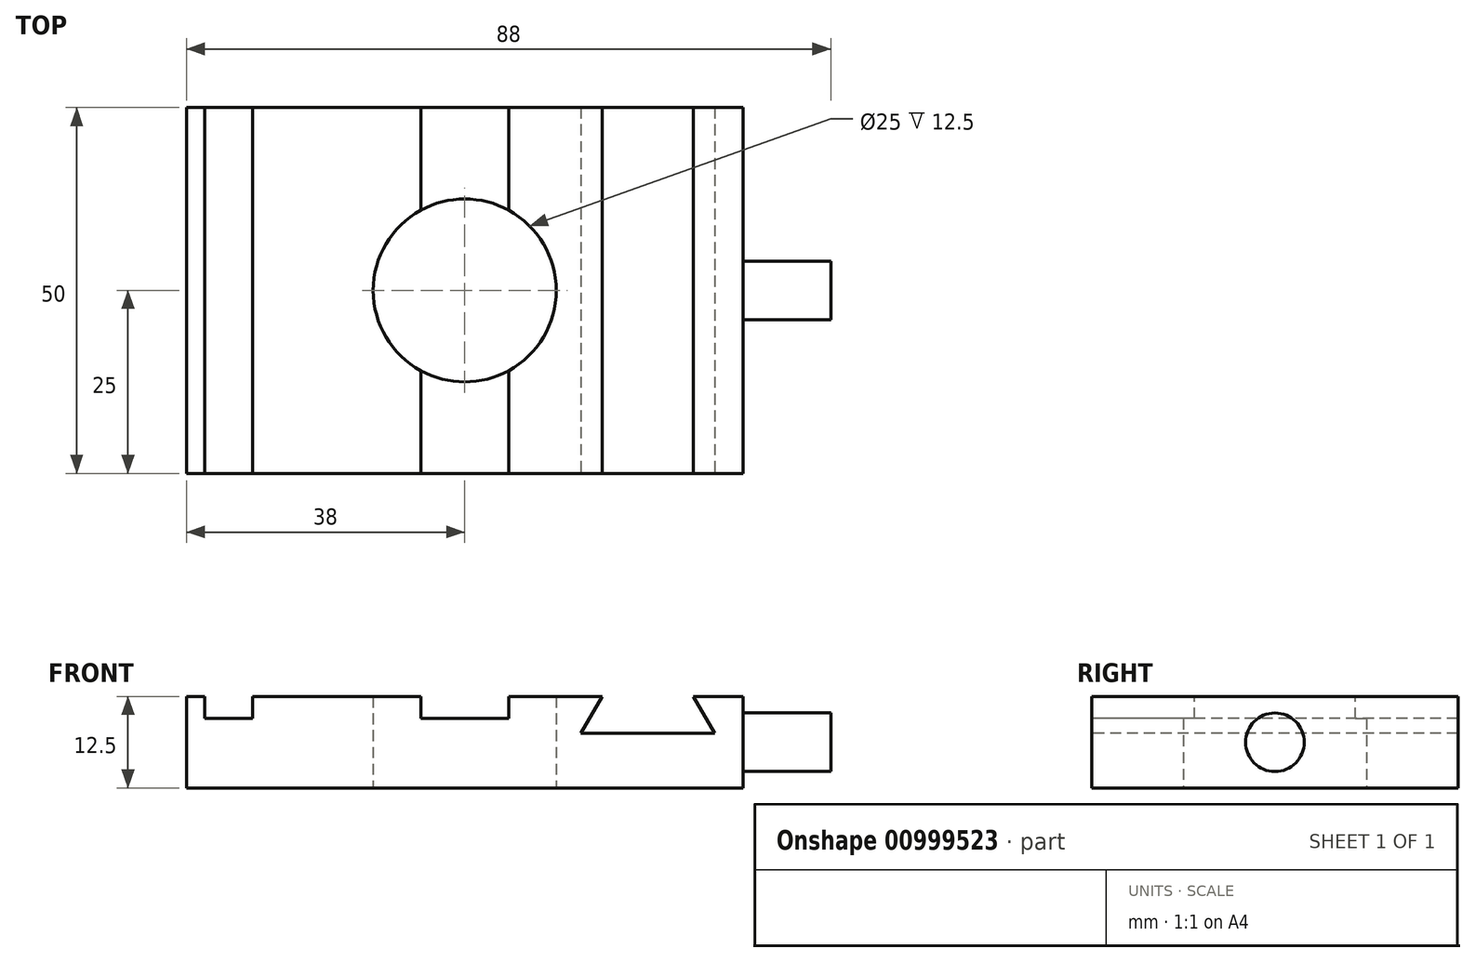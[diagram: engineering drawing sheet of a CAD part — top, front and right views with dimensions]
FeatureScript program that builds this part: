
annotation { "Feature Type Name" : "Feature", "Feature Type Description" : "" }
export const myFeature = defineFeature(function(context is Context, id is Id, definition is map)
    precondition{}
    {
        {
            var Q0;
            Q0=qCreatedBy(makeId("Top.planeOp"),FACE);
            var sketch = newSketch(context, id + "F0", { "sketchPlane" : qUnion([Q0])});
            skLineSegment(sketch, "E0.bottom", {"start": v(38, 25) * mm, "end": v(-38, 25) * mm});
            skLineSegment(sketch, "E0.top", {"start": v(38, -25) * mm, "end": v(-38, -25) * mm});
            skLineSegment(sketch, "E0.left", {"start": v(38, 25) * mm, "end": v(38, -25) * mm});
            skLineSegment(sketch, "E0.right", {"start": v(-38, 25) * mm, "end": v(-38, -25) * mm});
            skPoint(sketch, "E0.middle", {"position": v(0, 0) * mm});
            skCircle(sketch, "E1", {"center": v(0, 0) * mm, "radius": 12.5 * mm});
            skSolve(sketch);
        }
        {
            var Q0;
            Q0=makeQuery(id+"F0.imprint","IMPRINT",FACE,{"disambiguationData":[TD([[makeQuery(id+"F0.imprint","IMPRINT",EDGE,{"derivedFrom":sQuery(id+"F0.wireOp",EDGE,"E0.bottom")}),1.0]])]});
            extrude(context, id + "F1", {"entities" : qUnion([Q0]), "depth" : 12.5 * mm, "offsetDistance" : 25 * mm});
        }
        {
            var Q0;
            Q0=makeQuery(id+"F1.opExtrude","CAP_FACE",FACE,{"disambiguationData":[OSD([sQuery(id+"F0.wireOp",EDGE,"E0.bottom"),sQuery(id+"F0.wireOp",EDGE,"E0.top"),sQuery(id+"F0.wireOp",EDGE,"E0.left"),sQuery(id+"F0.wireOp",EDGE,"E0.right"),sQuery(id+"F0.wireOp",EDGE,"E1")])],"isStart":false});
            var sketch = newSketch(context, id + "F2", { "sketchPlane" : qUnion([Q0])});
            skLineSegment(sketch, "E2.bottom", {"start": v(-35.5, 25) * mm, "end": v(-29, 25) * mm});
            skLineSegment(sketch, "E2.top", {"start": v(-35.5, -25) * mm, "end": v(-29, -25) * mm});
            skLineSegment(sketch, "E2.left", {"start": v(-35.5, 25) * mm, "end": v(-35.5, -25) * mm});
            skLineSegment(sketch, "E2.right", {"start": v(-29, 25) * mm, "end": v(-29, -25) * mm});
            skLineSegment(sketch, "E3", {"start": v(-6, 25) * mm, "end": v(-6, -25) * mm});
            skLineSegment(sketch, "E4", {"start": v(-6, -25) * mm, "end": v(6, -25) * mm});
            skLineSegment(sketch, "E5", {"start": v(6, -25) * mm, "end": v(6, 25) * mm});
            skLineSegment(sketch, "E6", {"start": v(6, 25) * mm, "end": v(-6, 25) * mm});
            skPoint(sketch, "E7", {"position": v(0, 0) * mm});
            skLineSegment(sketch, "E8", {"start": v(0, 25) * mm, "end": v(0, -25) * mm, "construction": true});
            skSolve(sketch);
        }
        {
            var Q0;
            Q0=makeQuery(id+"F2.imprint","IMPRINT",FACE,{"disambiguationData":[TD([[makeQuery(id+"F2.imprint","IMPRINT",EDGE,{"derivedFrom":sQuery(id+"F2.wireOp",EDGE,"E2.bottom")}),1.0]])]});
            var Q1;
            {var subQ0=sQuery(id+"F2.wireOp",EDGE,"E6");Q1=makeQuery(id+"F2.imprint","IMPRINT",FACE,{"disambiguationData":[TD([[makeQuery(id+"F2.imprint","IMPRINT",EDGE,{"derivedFrom":subQ0}),1.0]])]});}
            var Q2;
            {var subQ0=sQuery(id+"F2.wireOp",EDGE,"E4");Q2=makeQuery(id+"F2.imprint","IMPRINT",FACE,{"disambiguationData":[TD([[makeQuery(id+"F2.imprint","IMPRINT",EDGE,{"derivedFrom":subQ0}),-1.0]])]});}
            extrude(context, id + "F3", {"entities" : qUnion([Q0, Q1, Q2]), "operationType" : NewBodyOperationType.REMOVE, "oppositeDirection" : true, "depth" : 3 * mm, "offsetDistance" : 25 * mm});
        }
        {
            var Q0;
            Q0=makeQuery(id+"F1.opExtrude","SWEPT_FACE",FACE,{"disambiguationData":[OSD([sQuery(id+"F0.wireOp",EDGE,"E0.top")])]});
            var sketch = newSketch(context, id + "F4", { "sketchPlane" : qUnion([Q0])});
            skLineSegment(sketch, "E9", {"start": v(18.75, 12.5) * mm, "end": v(15.86, 7.5) * mm});
            skLineSegment(sketch, "E10", {"start": v(15.86, 7.5) * mm, "end": v(34.14, 7.5) * mm});
            skLineSegment(sketch, "E11", {"start": v(34.14, 7.5) * mm, "end": v(31.25, 12.5) * mm});
            skLineSegment(sketch, "E12", {"start": v(31.25, 12.5) * mm, "end": v(18.75, 12.5) * mm});
            skLineSegment(sketch, "E13", {"start": v(25, 12.5) * mm, "end": v(25, 7.5) * mm, "construction": true});
            skSolve(sketch);
        }
        {
            var Q0;
            Q0 = qSketchRegion(id + "F4", true);
            extrude(context, id + "F5", {"entities" : qUnion([Q0]), "operationType" : NewBodyOperationType.REMOVE, "endBound" : BoundingType.UP_TO_NEXT, "oppositeDirection" : true, "depth" : 25 * mm, "offsetDistance" : 25 * mm});
        }
        {
            var Q0;
            Q0=makeQuery(id+"F1.opExtrude","SWEPT_FACE",FACE,{"disambiguationData":[OSD([sQuery(id+"F0.wireOp",EDGE,"E0.left")])]});
            var sketch = newSketch(context, id + "F6", { "sketchPlane" : qUnion([Q0])});
            skCircle(sketch, "E14", {"center": v(0, 6.25) * mm, "radius": 4 * mm});
            skPoint(sketch, "E14.centerSnap0", {"position": v(-25, 6.25) * mm});
            skPoint(sketch, "E14.centerSnap1", {"position": v(0, 12.5) * mm});
            skSolve(sketch);
        }
        {
            var Q0;
            Q0=makeQuery(id+"F6.imprint","IMPRINT",FACE,{"disambiguationData":[TD([[makeQuery(id+"F6.imprint","IMPRINT",EDGE,{"derivedFrom":sQuery(id+"F6.wireOp",EDGE,"E14")}),1.0]])]});
            extrude(context, id + "F7", {"entities" : qUnion([Q0]), "operationType" : NewBodyOperationType.ADD, "depth" : 12 * mm, "offsetDistance" : 25 * mm});
        }
    });
